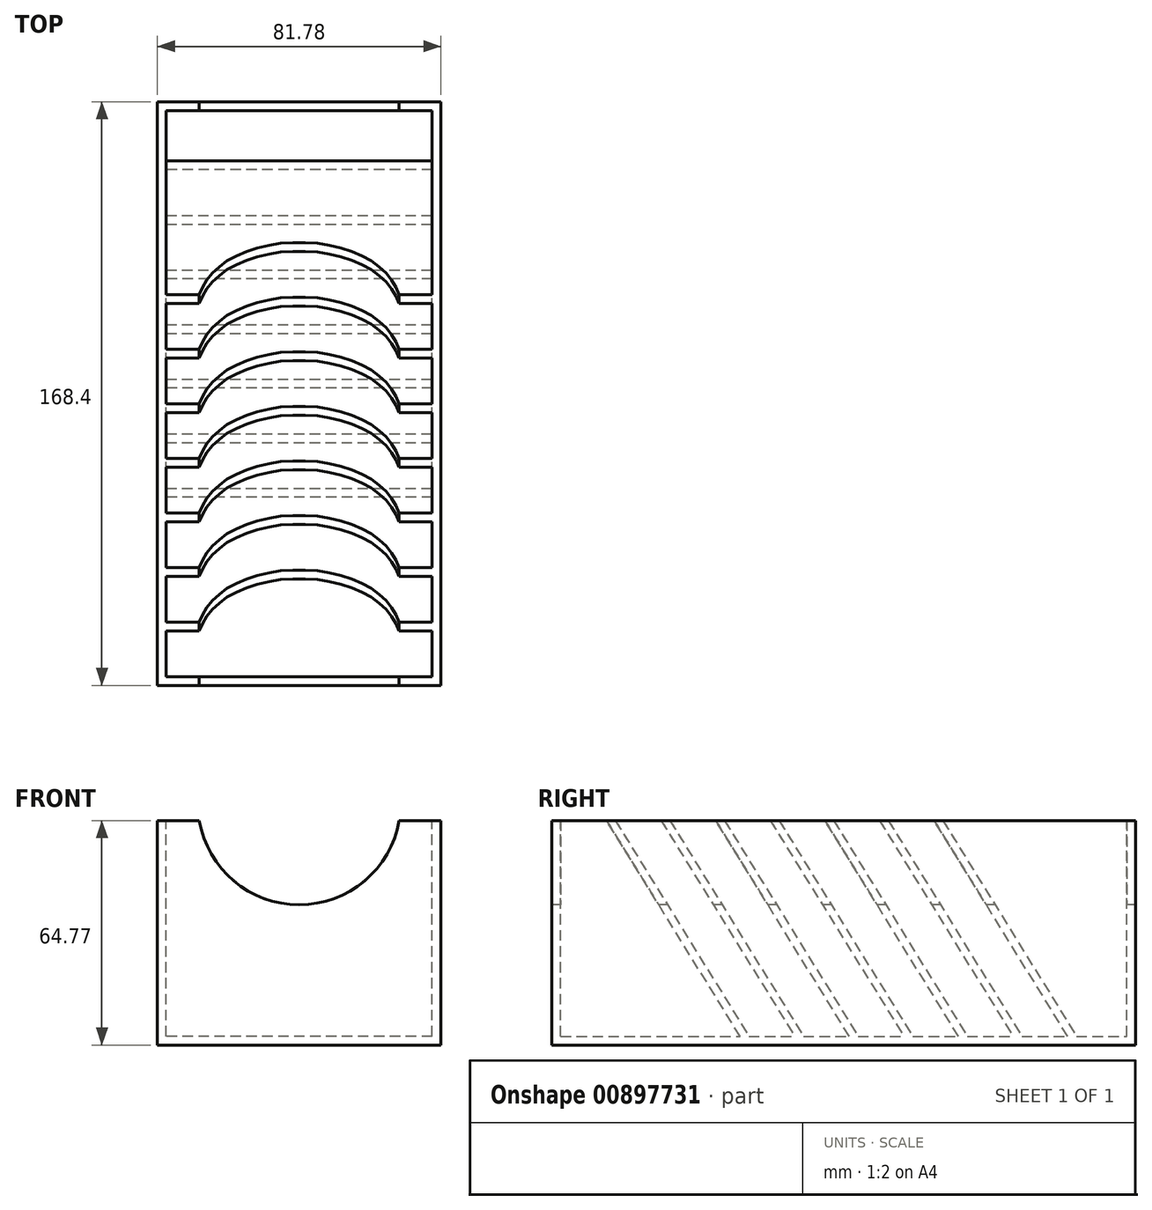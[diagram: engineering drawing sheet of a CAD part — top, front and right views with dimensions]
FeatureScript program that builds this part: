
annotation { "Feature Type Name" : "Feature", "Feature Type Description" : "" }
export const myFeature = defineFeature(function(context is Context, id is Id, definition is map)
    precondition{}
    {
        {
            var Q0;
            Q0=qCreatedBy(makeId("Top.planeOp"),FACE);
            var sketch = newSketch(context, id + "F0", { "sketchPlane" : qUnion([Q0])});
            skLineSegment(sketch, "E0.bottom", {"start": v(40.9, -84.2) * mm, "end": v(-40.9, -84.2) * mm});
            skLineSegment(sketch, "E0.top", {"start": v(40.9, 84.2) * mm, "end": v(-40.9, 84.2) * mm});
            skLineSegment(sketch, "E0.left", {"start": v(40.9, -84.2) * mm, "end": v(40.9, 84.2) * mm});
            skLineSegment(sketch, "E0.right", {"start": v(-40.9, -84.2) * mm, "end": v(-40.9, 84.2) * mm});
            skPoint(sketch, "E0.middle", {"position": v(0, 0) * mm});
            skSolve(sketch);
        }
        {
            var Q0;
            Q0 = qSketchRegion(id + "F0", true);
            extrude(context, id + "F1", {"entities" : qUnion([Q0]), "depth" : 64.77 * mm, "offsetDistance" : 25.4 * mm});
        }
        {
            var Q0;
            Q0=makeQuery(id+"F1.opExtrude","CAP_FACE",FACE,{"disambiguationData":[OSD([sQuery(id+"F0.wireOp",EDGE,"E0.bottom"),sQuery(id+"F0.wireOp",EDGE,"E0.top"),sQuery(id+"F0.wireOp",EDGE,"E0.left"),sQuery(id+"F0.wireOp",EDGE,"E0.right")])],"isStart":false});
            var sketch = newSketch(context, id + "F2", { "sketchPlane" : qUnion([Q0])});
            skLineSegment(sketch, "E1.bottom", {"start": v(38.35, -81.66) * mm, "end": v(-38.35, -81.66) * mm});
            skLineSegment(sketch, "E1.top", {"start": v(38.35, 81.66) * mm, "end": v(-38.35, 81.66) * mm});
            skLineSegment(sketch, "E1.left", {"start": v(38.35, -81.66) * mm, "end": v(38.35, 81.66) * mm});
            skLineSegment(sketch, "E1.right", {"start": v(-38.35, -81.66) * mm, "end": v(-38.35, 81.66) * mm});
            skPoint(sketch, "E1.middle", {"position": v(0, 0) * mm});
            skSolve(sketch);
        }
        {
            var Q0;
            Q0 = qSketchRegion(id + "F2", true);
            extrude(context, id + "F3", {"entities" : qUnion([Q0]), "operationType" : NewBodyOperationType.REMOVE, "oppositeDirection" : true, "depth" : 62.23 * mm, "offsetDistance" : 25.4 * mm});
        }
        {
            var Q0;
            Q0=makeQuery(id+"F1.opExtrude","SWEPT_FACE",FACE,{"disambiguationData":[OSD([sQuery(id+"F0.wireOp",EDGE,"E0.left")])]});
            var sketch = newSketch(context, id + "F4", { "sketchPlane" : qUnion([Q0])});
            skLineSegment(sketch, "E2", {"start": v(-84.2, 64.77) * mm, "end": v(-84.2, 0) * mm});
            skLineSegment(sketch, "E3", {"start": v(-84.2, 0) * mm, "end": v(-41.52, 0) * mm});
            skLineSegment(sketch, "E4", {"start": v(-41.52, 0) * mm, "end": v(-28.31, 0) * mm});
            skLineSegment(sketch, "E5", {"start": v(-28.31, 0) * mm, "end": v(-68.45, 64.77) * mm});
            skLineSegment(sketch, "E6", {"start": v(-68.45, 64.77) * mm, "end": v(-65.91, 64.77) * mm});
            skLineSegment(sketch, "E7", {"start": v(-65.91, 64.77) * mm, "end": v(-25.77, 0) * mm});
            skLineSegment(sketch, "E8", {"start": v(-25.77, 0) * mm, "end": v(-28.31, 0) * mm});
            skPoint(sketch, "E9.startSnap0", {"position": v(-75.06, 64.77) * mm});
            skLineSegment(sketch, "E10", {"start": v(-25.77, 0) * mm, "end": v(-12.56, 0) * mm});
            skLineSegment(sketch, "E11", {"start": v(-52.7, 64.77) * mm, "end": v(-50.16, 64.77) * mm});
            skLineSegment(sketch, "E12", {"start": v(-50.16, 64.77) * mm, "end": v(-10.02, 0) * mm});
            skLineSegment(sketch, "E13", {"start": v(-52.7, 64.77) * mm, "end": v(-12.56, 0) * mm});
            skLineSegment(sketch, "E14", {"start": v(-12.56, 0) * mm, "end": v(-10.02, 0) * mm});
            skLineSegment(sketch, "E15", {"start": v(-10.02, 0) * mm, "end": v(3.18, 0) * mm});
            skLineSegment(sketch, "E16", {"start": v(3.18, 0) * mm, "end": v(-36.96, 64.77) * mm});
            skLineSegment(sketch, "E17", {"start": v(-36.96, 64.77) * mm, "end": v(-34.42, 64.77) * mm});
            skLineSegment(sketch, "E18", {"start": v(-34.42, 64.77) * mm, "end": v(5.72, 0) * mm});
            skLineSegment(sketch, "E19", {"start": v(5.72, 0) * mm, "end": v(3.18, 0) * mm});
            skLineSegment(sketch, "E20", {"start": v(5.72, 0) * mm, "end": v(18.93, 0) * mm});
            skLineSegment(sketch, "E21", {"start": v(-21.2, 64.77) * mm, "end": v(-18.67, 64.77) * mm});
            skLineSegment(sketch, "E22", {"start": v(-18.67, 64.77) * mm, "end": v(21.47, 0) * mm});
            skLineSegment(sketch, "E23", {"start": v(-21.2, 64.77) * mm, "end": v(18.93, 0) * mm});
            skLineSegment(sketch, "E24", {"start": v(18.93, 0) * mm, "end": v(21.47, 0) * mm});
            skLineSegment(sketch, "E25", {"start": v(21.47, 0) * mm, "end": v(34.68, 0) * mm});
            skLineSegment(sketch, "E26", {"start": v(34.68, 0) * mm, "end": v(-5.46, 64.77) * mm});
            skLineSegment(sketch, "E27", {"start": v(-5.46, 64.77) * mm, "end": v(-2.92, 64.77) * mm});
            skLineSegment(sketch, "E28", {"start": v(-2.92, 64.77) * mm, "end": v(37.22, 0) * mm});
            skLineSegment(sketch, "E29", {"start": v(37.22, 0) * mm, "end": v(34.68, 0) * mm});
            skLineSegment(sketch, "E30", {"start": v(37.22, 0) * mm, "end": v(50.43, 0) * mm});
            skLineSegment(sketch, "E31", {"start": v(10.29, 64.77) * mm, "end": v(12.83, 64.77) * mm});
            skLineSegment(sketch, "E32", {"start": v(12.83, 64.77) * mm, "end": v(52.97, 0) * mm});
            skLineSegment(sketch, "E33", {"start": v(10.29, 64.77) * mm, "end": v(50.43, 0) * mm});
            skLineSegment(sketch, "E34", {"start": v(50.43, 0) * mm, "end": v(52.97, 0) * mm});
            skLineSegment(sketch, "E35", {"start": v(52.97, 0) * mm, "end": v(66.18, 0) * mm});
            skLineSegment(sketch, "E36", {"start": v(66.18, 0) * mm, "end": v(26.04, 64.77) * mm});
            skLineSegment(sketch, "E37", {"start": v(26.04, 64.77) * mm, "end": v(28.58, 64.77) * mm});
            skLineSegment(sketch, "E38", {"start": v(28.58, 64.77) * mm, "end": v(68.72, 0) * mm});
            skLineSegment(sketch, "E39", {"start": v(68.72, 0) * mm, "end": v(66.18, 0) * mm});
            skLineSegment(sketch, "E40", {"start": v(68.72, 0) * mm, "end": v(81.92, 0) * mm});
            skSolve(sketch);
        }
        {
            var Q0;
            Q0 = qSketchRegion(id + "F4", true);
            extrude(context, id + "F5", {"entities" : qUnion([Q0]), "operationType" : NewBodyOperationType.ADD, "oppositeDirection" : true, "depth" : 81.8 * mm, "offsetDistance" : 25.4 * mm});
        }
        {
            var Q0;
            Q0=makeQuery(id+"F1.opExtrude","SWEPT_FACE",FACE,{"disambiguationData":[OSD([sQuery(id+"F0.wireOp",EDGE,"E0.bottom")])]});
            var sketch = newSketch(context, id + "F6", { "sketchPlane" : qUnion([Q0])});
            skArc(sketch, "E41", {"start": v(-28.83, 64.77) * mm, "mid": v(0, 40.45) * mm, "end": v(28.83, 64.77) * mm});
            skLineSegment(sketch, "E42", {"start": v(-28.83, 64.77) * mm, "end": v(28.83, 64.77) * mm});
            skSolve(sketch);
        }
        {
            var Q0;
            Q0 = qSketchRegion(id + "F6", true);
            extrude(context, id + "F7", {"entities" : qUnion([Q0]), "operationType" : NewBodyOperationType.REMOVE, "oppositeDirection" : true, "depth" : 177.8 * mm, "offsetDistance" : 25.4 * mm});
        }
    });
